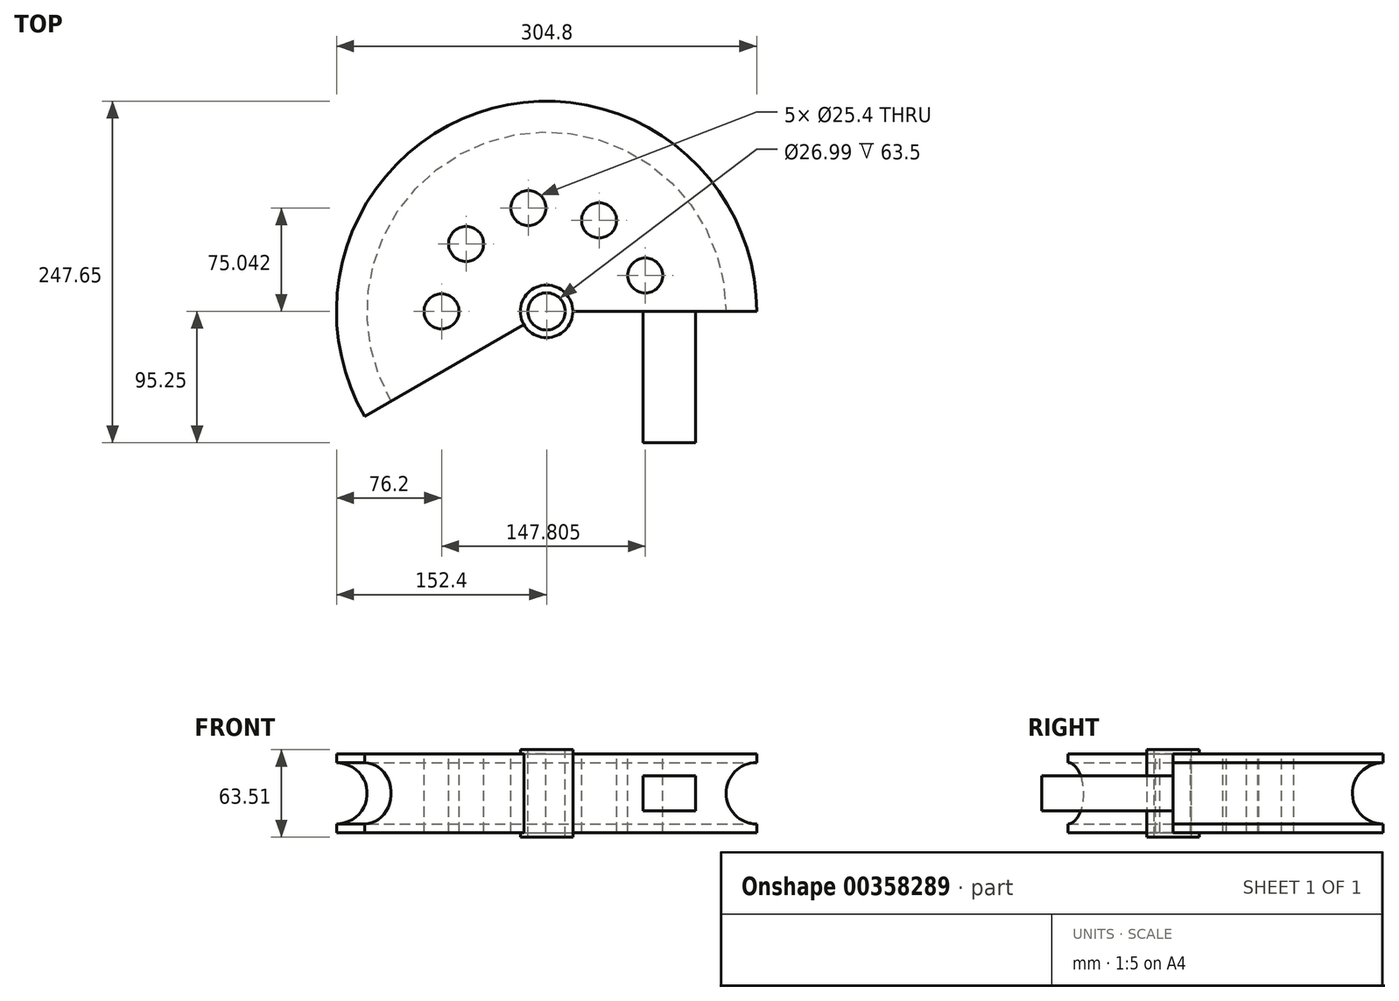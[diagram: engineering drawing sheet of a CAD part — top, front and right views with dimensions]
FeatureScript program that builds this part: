
annotation { "Feature Type Name" : "Feature", "Feature Type Description" : "" }
export const myFeature = defineFeature(function(context is Context, id is Id, definition is map)
    precondition{}
    {
        {
            var Q0;
            Q0=qCreatedBy(makeId("Front.planeOp"),FACE);
            var sketch = newSketch(context, id + "F0", { "sketchPlane" : qUnion([Q0])});
            skLineSegment(sketch, "E0.bottom", {"start": v(19.05, 0) * mm, "end": v(152.4, 0) * mm});
            skLineSegment(sketch, "E0.top", {"start": v(19.05, 57.15) * mm, "end": v(152.4, 57.15) * mm});
            skLineSegment(sketch, "E0.left", {"start": v(0, 0) * mm, "end": v(0, 57.15) * mm});
            skLineSegment(sketch, "E0.right", {"start": v(152.4, 0) * mm, "end": v(152.4, 6.35) * mm});
            skArc(sketch, "E1", {"start": v(152.4, 50.8) * mm, "mid": v(130.18, 28.58) * mm, "end": v(152.4, 6.35) * mm});
            skLineSegment(sketch, "E2.bottom", {"start": v(0, 60.33) * mm, "end": v(19.05, 60.33) * mm});
            skLineSegment(sketch, "E2.top", {"start": v(0, -3.18) * mm, "end": v(19.05, -3.18) * mm});
            skLineSegment(sketch, "E2.left", {"start": v(0, 60.33) * mm, "end": v(0, 57.15) * mm});
            skLineSegment(sketch, "E2.right", {"start": v(19.05, 60.33) * mm, "end": v(19.05, -3.17) * mm});
            skLineSegment(sketch, "E3.trimOffspring", {"start": v(0, 0) * mm, "end": v(0, -3.17) * mm});
            skLineSegment(sketch, "E4.trimOffspring", {"start": v(152.4, 50.8) * mm, "end": v(152.4, 57.15) * mm});
            skSolve(sketch);
        }
        {
            var Q0;
            Q0 = qSketchRegion(id + "F0", true);
            var Q1;
            Q1=sQuery(id+"F0.wireOp",EDGE,"E0.left");
            revolve(context, id + "F1", {"entities" : qUnion([Q0]), "axis" : qUnion([Q1]), "revolveType" : RevolveType.ONE_DIRECTION, "angle" : 210 * degree});
        }
        {
            var Q0;
            Q0=makeQuery(id+"F1.opRevolve","SWEPT_FACE",FACE,{"disambiguationData":[OSD([sQuery(id+"F0.wireOp",EDGE,"E2.bottom")])]});
            var sketch = newSketch(context, id + "F2", { "sketchPlane" : qUnion([Q0])});
            skCircle(sketch, "E5", {"center": v(0, 0) * mm, "radius": 13.5 * mm});
            skSolve(sketch);
        }
        {
            var Q0;
            Q0 = qSketchRegion(id + "F2", true);
            extrude(context, id + "F3", {"entities" : qUnion([Q0]), "operationType" : NewBodyOperationType.REMOVE, "oppositeDirection" : true, "depth" : 69.85 * mm});
        }
        {
            var Q0;
            Q0=makeQuery(id+"F1.opRevolve","SWEPT_FACE",FACE,{"disambiguationData":[OSD([sQuery(id+"F0.wireOp",EDGE,"E0.top")])]});
            var sketch = newSketch(context, id + "F4", { "sketchPlane" : qUnion([Q0])});
            skCircle(sketch, "E6", {"center": v(-76.2, 0) * mm, "radius": 12.7 * mm});
            skCircle(sketch, "E7.1.0", {"center": v(-58.37, 48.98) * mm, "radius": 12.7 * mm});
            skCircle(sketch, "E7.2.0", {"center": v(-13.23, 75.04) * mm, "radius": 12.7 * mm});
            skCircle(sketch, "E7.3.0", {"center": v(38.1, 66) * mm, "radius": 12.7 * mm});
            skCircle(sketch, "E7.4.0", {"center": v(71.6, 26.06) * mm, "radius": 12.7 * mm});
            skPoint(sketch, "E7.center", {"position": v(0, 0) * mm});
            skLineSegment(sketch, "E7.anchor1", {"start": v(0, 0) * mm, "end": v(-76.2, 0) * mm, "construction": true});
            skLineSegment(sketch, "E7.anchor2", {"start": v(0, 0) * mm, "end": v(71.6, 26.06) * mm, "construction": true});
            skSolve(sketch);
        }
        {
            var Q0;
            Q0 = qSketchRegion(id + "F4", true);
            extrude(context, id + "F5", {"entities" : qUnion([Q0]), "operationType" : NewBodyOperationType.REMOVE, "oppositeDirection" : true, "depth" : 63.5 * mm});
        }
        {
            var Q0;
            Q0=makeQuery(id+"F1.opRevolve","CAP_FACE",FACE,{"disambiguationData":[OSD([sQuery(id+"F0.wireOp",EDGE,"E0.bottom"),sQuery(id+"F0.wireOp",EDGE,"E0.top"),sQuery(id+"F0.wireOp",EDGE,"E0.left"),sQuery(id+"F0.wireOp",EDGE,"E0.right"),sQuery(id+"F0.wireOp",EDGE,"E1"),sQuery(id+"F0.wireOp",EDGE,"E2.bottom"),sQuery(id+"F0.wireOp",EDGE,"E2.top"),sQuery(id+"F0.wireOp",EDGE,"E2.left"),sQuery(id+"F0.wireOp",EDGE,"E2.right"),sQuery(id+"F0.wireOp",EDGE,"E3.trimOffspring"),sQuery(id+"F0.wireOp",EDGE,"E4.trimOffspring")])],"isStart":true});
            var sketch = newSketch(context, id + "F6", { "sketchPlane" : qUnion([Q0])});
            skLineSegment(sketch, "E8.bottom", {"start": v(69.85, 41.27) * mm, "end": v(107.95, 41.27) * mm});
            skLineSegment(sketch, "E8.top", {"start": v(69.85, 15.87) * mm, "end": v(107.95, 15.88) * mm});
            skLineSegment(sketch, "E8.left", {"start": v(69.85, 41.27) * mm, "end": v(69.85, 15.87) * mm});
            skLineSegment(sketch, "E8.right", {"start": v(107.95, 41.28) * mm, "end": v(107.95, 15.88) * mm});
            skSolve(sketch);
        }
        {
            var Q0;
            Q0 = qSketchRegion(id + "F6", true);
            extrude(context, id + "F7", {"entities" : qUnion([Q0]), "operationType" : NewBodyOperationType.ADD, "depth" : 95.25 * mm});
        }
        {
            var Q0;
            Q0=makeQuery(id+"F1.opRevolve","SWEPT_FACE",FACE,{"disambiguationData":[OSD([sQuery(id+"F0.wireOp",EDGE,"E2.bottom")])]});
            var sketch = newSketch(context, id + "F8", { "sketchPlane" : qUnion([Q0])});
            skCircle(sketch, "E9", {"center": v(0, 0) * mm, "radius": 13.5 * mm});
            skCircle(sketch, "E10", {"center": v(0, 0) * mm, "radius": 19.05 * mm});
            skSolve(sketch);
        }
        {
            var Q0;
            Q0 = qSketchRegion(id + "F8", true);
            extrude(context, id + "F9", {"entities" : qUnion([Q0]), "operationType" : NewBodyOperationType.ADD, "oppositeDirection" : true, "depth" : 63.5 * mm});
        }
    });
